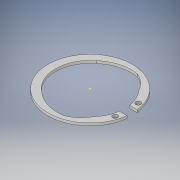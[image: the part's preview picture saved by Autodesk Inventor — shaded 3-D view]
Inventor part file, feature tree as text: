
AUTODESK INVENTOR PART (.ipt)
format: ipt  version: 2018 (Build 220112000, 112)  size: 136,704 bytes
history: native  units: in
note: dims shown in document units (in); Inventor stores cm internally (conversion verified against a paired STEP export)
features: sketch x2, extrude x1
ambient origin geometry x8: Origin, YZ Plane, XZ Plane, XY Plane, X Axis, Y Axis, Z Axis, Center Point
bodies: Solid1 (feature_tree)
feature tree (3):
  extrude  "Extrusion1"  Depth=1.671in
  sketch  "Sketch2"  dims[d2=0.025in d3=0.025in d4=0.1in d5=0.169in d6=1.503in d7=0.05in d8=0.0in d9=0.744in d10=1.372in d11=0.17in d12=0.1in d13=0.085in d14=0.17in d15=0.015in d16=0.015in]
  sketch  "Sketch1"  dims[d0=1.333in d1=1.671in]
